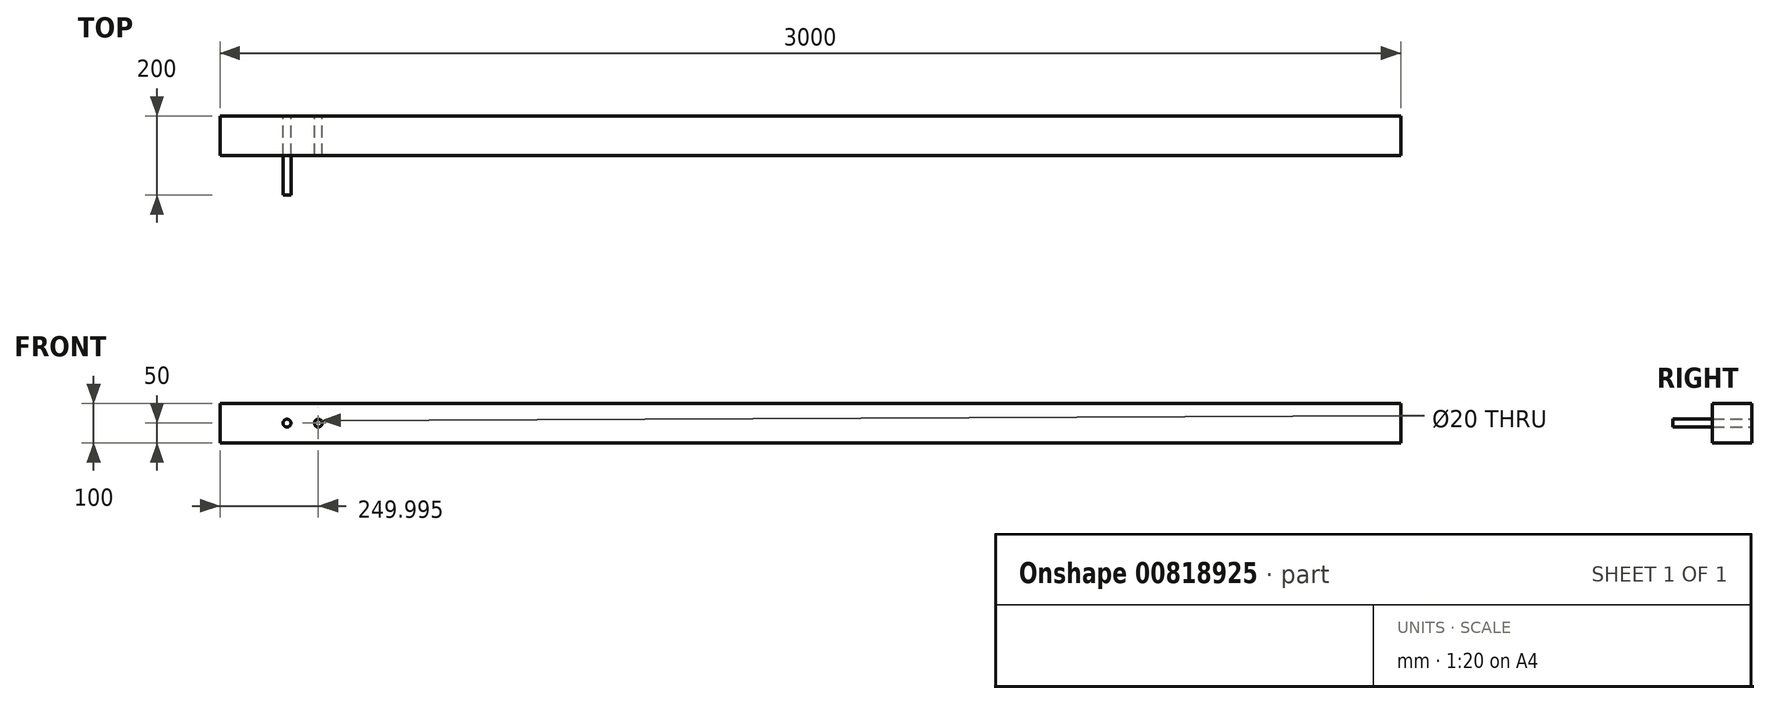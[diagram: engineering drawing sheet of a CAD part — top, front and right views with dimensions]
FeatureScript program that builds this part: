
annotation { "Feature Type Name" : "Feature", "Feature Type Description" : "" }
export const myFeature = defineFeature(function(context is Context, id is Id, definition is map)
    precondition{}
    {
        {
            var Q0;
            Q0=qCreatedBy(makeId("Front.planeOp"),FACE);
            var sketch = newSketch(context, id + "F0", { "sketchPlane" : qUnion([Q0])});
            skLineSegment(sketch, "E0.bottom", {"start": v(-170.33, 50) * mm, "end": v(2829.67, 50) * mm});
            skLineSegment(sketch, "E0.top", {"start": v(-170.33, -50) * mm, "end": v(2829.67, -50) * mm});
            skLineSegment(sketch, "E0.left", {"start": v(-170.33, 50) * mm, "end": v(-170.33, -50) * mm});
            skLineSegment(sketch, "E0.right", {"start": v(2829.67, 50) * mm, "end": v(2829.67, -50) * mm});
            skPoint(sketch, "E1", {"position": v(79.67, 0) * mm});
            skSolve(sketch);
        }
        {
            var Q0;
            Q0=makeQuery(id+"F0.imprint","IMPRINT",FACE,{"disambiguationData":[TD([[makeQuery(id+"F0.imprint","IMPRINT",EDGE,{"derivedFrom":sQuery(id+"F0.wireOp",EDGE,"E0.bottom")}),-1.0]])]});
            extrude(context, id + "F1", {"entities" : qUnion([Q0]), "depth" : 100 * mm, "offsetDistance" : 25 * mm});
        }
        {
            var Q0;
            Q0=sQuery(id+"F0.wireOp",VERTEX,"E1");
            var Q1;
            Q1=makeQuery(id+"F1.opExtrude","SWEPT_BODY",BODY,{"disambiguationData":[OSD([sQuery(id+"F0.wireOp",EDGE,"E0.bottom"),sQuery(id+"F0.wireOp",EDGE,"E0.top"),sQuery(id+"F0.wireOp",EDGE,"E0.left"),sQuery(id+"F0.wireOp",EDGE,"E0.right")])]});
            hole(context, id + "F2", {"style" : HoleStyle.SIMPLE, "endStyle" : HoleEndStyle.THROUGH, "oppositeDirection" : true, "holeDiameter" : 20 * mm, "majorDiameter" : 5 * mm, "isTappedThrough" : true, "tappedDepth" : 12 * mm, "tapClearance" : 3, "locations" : qUnion([Q0]), "scope" : qUnion([Q1])});
        }
        {
            var Q0;
            Q0=qCreatedBy(makeId("Front.planeOp"),FACE);
            var sketch = newSketch(context, id + "F3", { "sketchPlane" : qUnion([Q0])});
            skCircle(sketch, "E2", {"center": v(0, 0) * mm, "radius": 10 * mm});
            skSolve(sketch);
        }
        {
            var Q0;
            Q0=makeQuery(id+"F3.imprint","IMPRINT",FACE,{"disambiguationData":[TD([[makeQuery(id+"F3.imprint","IMPRINT",EDGE,{"derivedFrom":sQuery(id+"F3.wireOp",EDGE,"E2")}),1.0]])]});
            extrude(context, id + "F4", {"entities" : qUnion([Q0]), "depth" : 200 * mm, "offsetDistance" : 25 * mm});
        }
    });
